# Revit family: Haworth_9_CollaborativeTable
name_source: partatom
category: Furniture
revit_build: Autodesk Revit 2018 (Build: 20170223_1515(x64)
units: mm (PartAtom-declared; Revit-internal decimal feet)

## family parameters
Always vertical = Yes
Cut with Voids When Loaded = No
OmniClass Number = 23.40.70.14.64.21
OmniClass Title = Systems Furniture
Room Calculation Point = No
Shared = No
Work Plane-Based = No

## types (2) — shared parameters
Actual Height = 28.7 "
Assembly Code = E2020200
Bottom Base = 6.7 "
Description = Haworth - Cassina - 9 - Collaborative Table
Manufacturer = Haworth
Model = Haworth - Cassina - 9
Revision Number = 1
Size = Verify Final Dim. w/ Haworth
Sustainability Info = https://www.haworth.com
URL = https://www.haworth.com
URL - Product = https://www.haworth.com
Warranty = http://www.haworth.com

## per-type parameters (varying)
| type | Actual Depth | Actual Diameter | Inner Diameter | Large | Outer Diameter | Small |
| Large Stone Base | 43.3 " | 43.3 " | 20.05 " | Yes | 21.65 " | No |
| Small Stone Base | 33.5 " | 33.5 " | 15.05 " | No | 16.75 " | Yes |

## geometry (parser evidence)
native form markers: Sweep x6
no freeform markers — native parametric forms only
